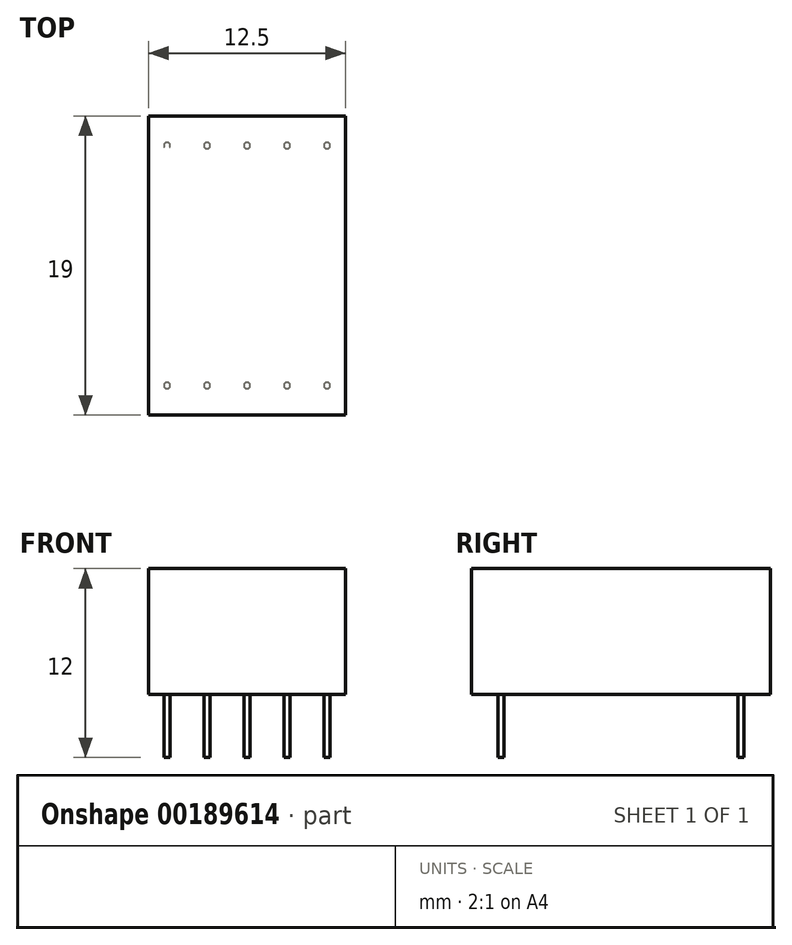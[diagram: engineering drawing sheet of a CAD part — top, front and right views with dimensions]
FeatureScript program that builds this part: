
annotation { "Feature Type Name" : "Feature", "Feature Type Description" : "" }
export const myFeature = defineFeature(function(context is Context, id is Id, definition is map)
    precondition{}
    {
        {
            var Q0;
            Q0=qCreatedBy(makeId("Top.planeOp"),FACE);
            var sketch = newSketch(context, id + "F0", { "sketchPlane" : qUnion([Q0])});
            skLineSegment(sketch, "E0.bottom", {"start": v(6.25, 9.5) * mm, "end": v(-6.25, 9.5) * mm});
            skLineSegment(sketch, "E0.top", {"start": v(6.25, -9.5) * mm, "end": v(-6.25, -9.5) * mm});
            skLineSegment(sketch, "E0.left", {"start": v(6.25, 9.5) * mm, "end": v(6.25, -9.5) * mm});
            skLineSegment(sketch, "E0.right", {"start": v(-6.25, 9.5) * mm, "end": v(-6.25, -9.5) * mm});
            skPoint(sketch, "E0.middle", {"position": v(0, 0) * mm});
            skSolve(sketch);
        }
        {
            var Q0;
            Q0=qSketchRegion(id+"F0",true);
            extrude(context, id + "F1", {"entities" : qUnion([Q0]), "depth" : 8 * mm});
        }
        {
            var Q0;
            Q0=makeQuery(id+"F1.opExtrude","CAP_FACE",FACE,{"disambiguationData":[OSD([sQuery(id+"F0.wireOp",EDGE,"E0.bottom"),sQuery(id+"F0.wireOp",EDGE,"E0.top"),sQuery(id+"F0.wireOp",EDGE,"E0.left"),sQuery(id+"F0.wireOp",EDGE,"E0.right")])],"isStart":true});
            var sketch = newSketch(context, id + "F2", { "sketchPlane" : qUnion([Q0])});
            skCircle(sketch, "E1", {"center": v(-5.08, -7.62) * mm, "radius": 0.2 * mm});
            skCircle(sketch, "E2.0.1.0", {"center": v(-5.08, 7.62) * mm, "radius": 0.2 * mm});
            skCircle(sketch, "E2.1.0.0", {"center": v(-2.54, -7.62) * mm, "radius": 0.2 * mm});
            skCircle(sketch, "E2.1.1.0", {"center": v(-2.54, 7.62) * mm, "radius": 0.2 * mm});
            skCircle(sketch, "E2.2.0.0", {"center": v(0, -7.62) * mm, "radius": 0.2 * mm});
            skCircle(sketch, "E2.2.1.0", {"center": v(0, 7.62) * mm, "radius": 0.2 * mm});
            skCircle(sketch, "E2.3.0.0", {"center": v(2.54, -7.62) * mm, "radius": 0.2 * mm});
            skCircle(sketch, "E2.3.1.0", {"center": v(2.54, 7.62) * mm, "radius": 0.2 * mm});
            skCircle(sketch, "E2.4.0.0", {"center": v(5.08, -7.62) * mm, "radius": 0.2 * mm});
            skCircle(sketch, "E2.4.1.0", {"center": v(5.08, 7.62) * mm, "radius": 0.2 * mm});
            skLineSegment(sketch, "E2.direction1", {"start": v(-5.08, -7.62) * mm, "end": v(-2.54, -7.62) * mm, "construction": true});
            skLineSegment(sketch, "E2.direction2", {"start": v(-5.08, -7.62) * mm, "end": v(-5.08, 7.62) * mm, "construction": true});
            skSolve(sketch);
        }
        {
            var Q0;
            Q0=qSketchRegion(id+"F2",true);
            extrude(context, id + "F3", {"entities" : qUnion([Q0]), "operationType" : NewBodyOperationType.ADD, "depth" : 4 * mm});
        }
    });
